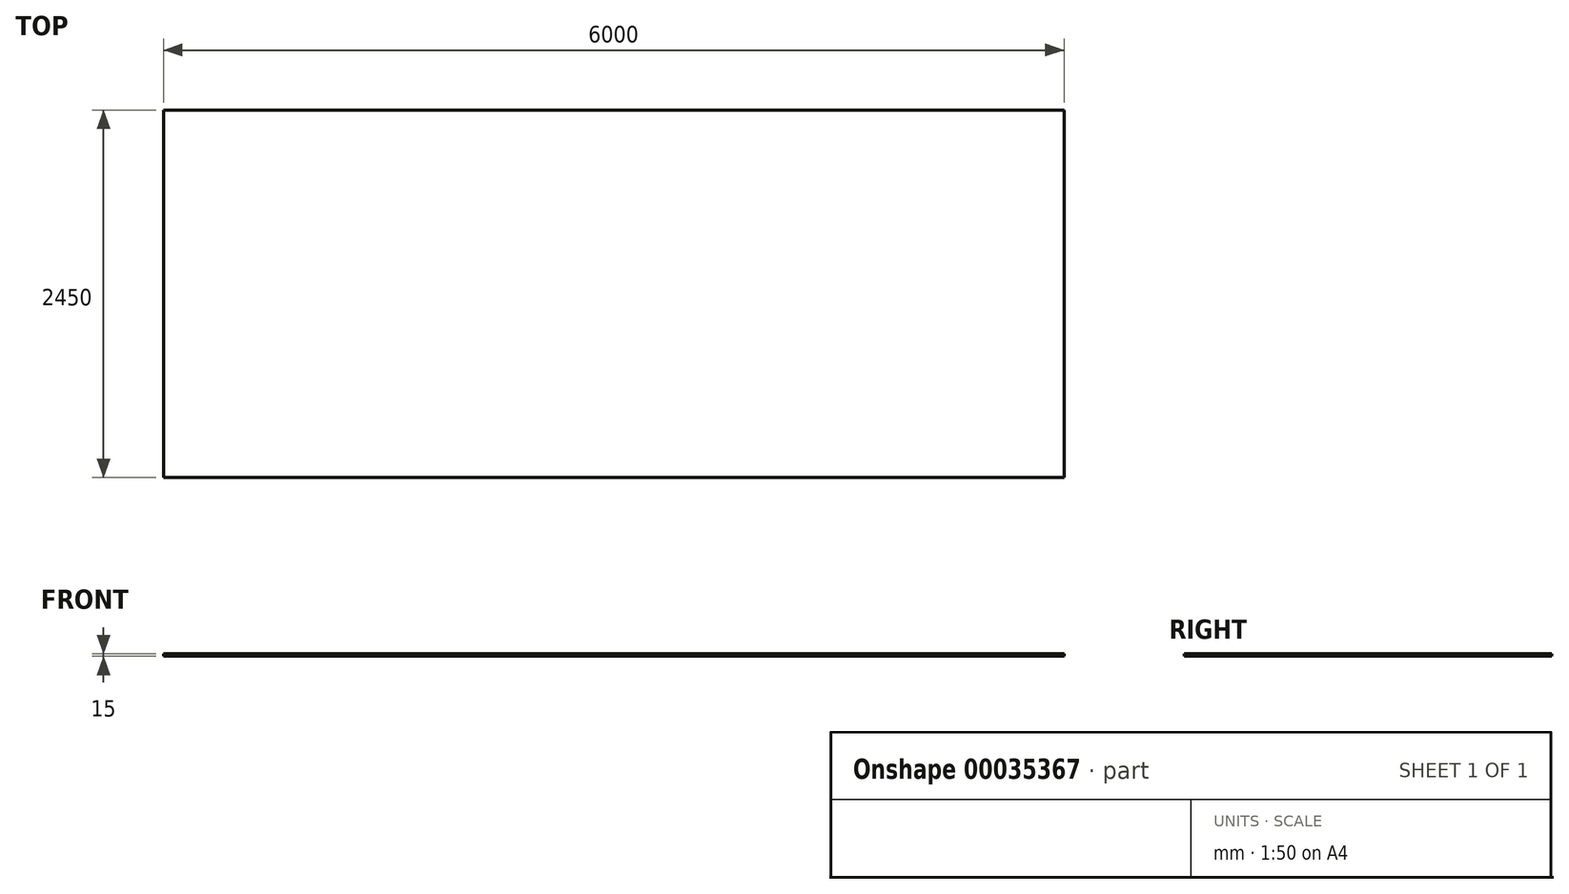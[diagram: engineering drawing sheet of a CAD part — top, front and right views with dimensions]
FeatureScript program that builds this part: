
annotation { "Feature Type Name" : "Feature", "Feature Type Description" : "" }
export const myFeature = defineFeature(function(context is Context, id is Id, definition is map)
    precondition{}
    {
        {
            var Q0;
            Q0=qCreatedBy(makeId("Top.planeOp"),FACE);
            var sketch = newSketch(context, id + "F0", { "sketchPlane" : qUnion([Q0])});
            skLineSegment(sketch, "E0.rect.bottom", {"start": v(3000, -1225) * mm, "end": v(-3000, -1225) * mm});
            skLineSegment(sketch, "E0.rect.top", {"start": v(3000, 1225) * mm, "end": v(-3000, 1225) * mm});
            skLineSegment(sketch, "E0.rect.left", {"start": v(3000, -1225) * mm, "end": v(3000, 1225) * mm});
            skLineSegment(sketch, "E0.rect.right", {"start": v(-3000, -1225) * mm, "end": v(-3000, 1225) * mm});
            skPoint(sketch, "E0.rect.middle", {"position": v(0, 0) * mm});
            skSolve(sketch);
        }
        {
            var Q0;
            Q0=makeQuery(id+"F0.imprint","IMPRINT",FACE,{"disambiguationData":[TD([[makeQuery(id+"F0.imprint","IMPRINT",EDGE,{"derivedFrom":sQuery(id+"F0.wireOp",EDGE,"E0.rect.bottom")}),-1.0]])]});
            extrude(context, id + "F1", {"entities" : qUnion([Q0]), "depth" : 15 * mm});
        }
    });
